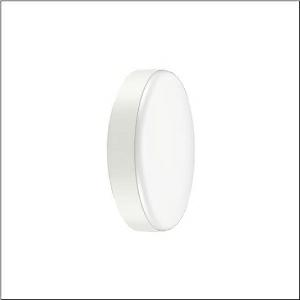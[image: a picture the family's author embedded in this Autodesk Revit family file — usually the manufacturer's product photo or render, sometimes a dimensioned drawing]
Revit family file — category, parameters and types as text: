
# Revit family: round_31_51wc10db34as
name_source: partatom
category: Lighting Fixtures
units: mm (PartAtom-declared; Revit-internal decimal feet)

## family parameters
Cut with Voids When Loaded = No
Host = Face
Light Source = No
Part Type = Normal
Room Calculation Point = No
Round Connector Dimension = Use Diameter
Shared = No

## types (1)
- Round 31 (1 x LED, 4250 lm, 35.4 W, 3000K)
    Apparent Load = 35 VA
    CIE Flux Codes = 44 75 94 94 100
    Color Rendering = 80
    Color Temperature = 3000K
    Default Elevation = 1800 mm
    Description = Round 31, wall and ceiling luminaire, primary optical cover: cover, of PC, opal, light emission: direct distribution, primary light characteristic: symmetric, installation type: surface-mounted, LED, rated luminous flux: 4.250lm, luminous efficacy: 120lm/W, light colour: 830, colour temperature: 3000K, control gear: DALI 2, with terminal, 5-pole, max. 2.5mm², mains connection: 220..240V, AC, 50/60Hz, rated input power: 35.5W, luminaire housing, of PC, traffic white (RAL 9016), diameter: 480mm, brightness and presence sensor, HF sensor, protection rating (complete): IP65, insulation class (complete): insulation class II (safety insulation), certification: CE, impact resistance: IK10, permissible operating ambient temperature: -20..+40°C, permissible storage temperature: -20..+60°C, packaging unit: 1 piece
    Height = 97 mm
    Lamp = 1 x LED
    Lamp Light Flux = 4250 lm
    Lamp Power = 35.4 W
    Lamp count = 1
    Length = 480 mm
    Luminous efficacy = 120 lm/W
    Manufacturer = Siteco
    ModVariant = No
    Model = 51WC10DB34AS
    Mounting Place = Ceiling
    Mounting Type = Surface mounted
    Number of Poles = 1
    OnlyDefault = Yes
    Power Factor = 1
    Product Name = Round 31
    Product group = wall and ceiling luminaire
    ProductGroupID = 304
    Protection Class = Protection class II
    Protection Degree = IP 65
    RLX_Detail_Level = 1
    RLX_Emergency_Light_Flux = 0 lm
    RLX_Emergency_Type = 0
    RLX_Emergency_Type_DB = No
    RlxData = <blob elided: 40921 chars, md5=18d50187>
    Socket = socket
    Standby Power = 0 W
    System Light Flux = 4250 lm
    System Power = 35 W
    Type Comments = Product without accessories
    Type Image = l_1007188.jpg
    URL = http://relux.com
    VarID = ---
    Voltage = 0 V
    Weight = 0.00 kg
    Width = 0 mm  [stored 0 ft]

note: [stored X ft] marks values corroborated as IEEE doubles in the binary element streams (Revit-internal decimal feet)

## geometry (parser evidence)
native form markers: Blend x4, Sweep x13
no freeform markers — native parametric forms only
